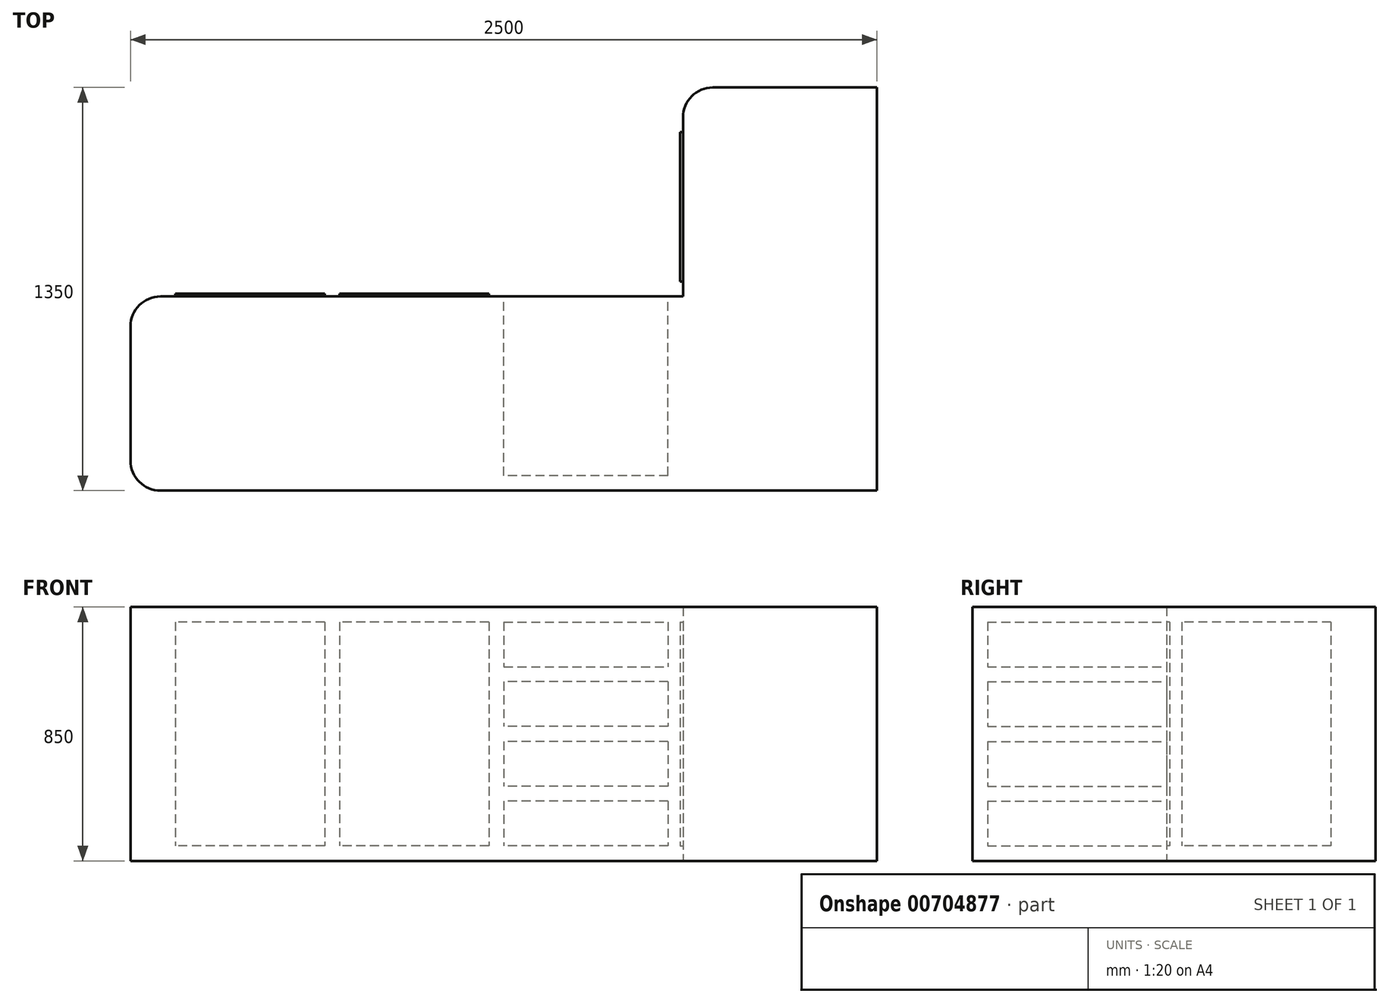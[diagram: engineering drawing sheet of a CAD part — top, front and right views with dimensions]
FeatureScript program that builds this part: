
annotation { "Feature Type Name" : "Feature", "Feature Type Description" : "" }
export const myFeature = defineFeature(function(context is Context, id is Id, definition is map)
    precondition{}
    {
        {
            var Q0;
            Q0=qCreatedBy(makeId("Top.planeOp"),FACE);
            var sketch = newSketch(context, id + "F0", { "sketchPlane" : qUnion([Q0])});
            skLineSegment(sketch, "E0", {"start": v(0, 0) * mm, "end": v(-2400, 0) * mm});
            skLineSegment(sketch, "E1", {"start": v(-2500, 100) * mm, "end": v(-2500, 550) * mm});
            skLineSegment(sketch, "E2", {"start": v(-2400, 650) * mm, "end": v(-650, 650) * mm});
            skLineSegment(sketch, "E3", {"start": v(-650, 650) * mm, "end": v(-650, 1250) * mm});
            skLineSegment(sketch, "E4", {"start": v(-550, 1350) * mm, "end": v(0, 1350) * mm});
            skLineSegment(sketch, "E5", {"start": v(0, 1350) * mm, "end": v(0, 0) * mm});
            skPoint(sketch, "E6.visualSharp", {"position": v(-650, 650) * mm});
            skPoint(sketch, "E7.visualSharp", {"position": v(-650, 1350) * mm});
            skArc(sketch, "E7.filletArc", {"start": v(-550, 1350) * mm, "mid": v(-620.71, 1320.71) * mm, "end": v(-650, 1250) * mm});
            skPoint(sketch, "E8.visualSharp", {"position": v(-2500, 650) * mm});
            skArc(sketch, "E8.filletArc", {"start": v(-2400, 650) * mm, "mid": v(-2470.71, 620.71) * mm, "end": v(-2500, 550) * mm});
            skPoint(sketch, "E9.visualSharp", {"position": v(-2500, 0) * mm});
            skArc(sketch, "E9.filletArc", {"start": v(-2500, 100) * mm, "mid": v(-2470.71, 29.29) * mm, "end": v(-2400, 0) * mm});
            skSolve(sketch);
        }
        {
            var Q0;
            Q0=makeQuery(id+"F0.imprint","IMPRINT",FACE,{"disambiguationData":[TD([[makeQuery(id+"F0.imprint","IMPRINT",EDGE,{"derivedFrom":sQuery(id+"F0.wireOp",EDGE,"E0")}),-1.0]])]});
            extrude(context, id + "F1", {"entities" : qUnion([Q0]), "depth" : 850 * mm, "offsetDistance" : 25 * mm});
        }
        {
            var Q0;
            Q0=makeQuery(id+"F1.opExtrude","SWEPT_FACE",FACE,{"disambiguationData":[OSD([sQuery(id+"F0.wireOp",EDGE,"E2")])]});
            var sketch = newSketch(context, id + "F2", { "sketchPlane" : qUnion([Q0])});
            skPoint(sketch, "E10.oppositeSnap0", {"position": v(1525, 0) * mm});
            skLineSegment(sketch, "E11.bottom", {"start": v(1300, 800) * mm, "end": v(1800, 800) * mm});
            skLineSegment(sketch, "E11.top", {"start": v(1300, 50) * mm, "end": v(1800, 50) * mm});
            skLineSegment(sketch, "E11.left", {"start": v(1300, 800) * mm, "end": v(1300, 50) * mm});
            skLineSegment(sketch, "E11.right", {"start": v(1800, 800) * mm, "end": v(1800, 50) * mm});
            skLineSegment(sketch, "E12.bottom", {"start": v(1850, 800) * mm, "end": v(2350, 800) * mm});
            skLineSegment(sketch, "E12.top", {"start": v(1850, 50) * mm, "end": v(2350, 50) * mm});
            skLineSegment(sketch, "E12.left", {"start": v(1850, 800) * mm, "end": v(1850, 50) * mm});
            skLineSegment(sketch, "E12.right", {"start": v(2350, 800) * mm, "end": v(2350, 50) * mm});
            skLineSegment(sketch, "E13.bottom", {"start": v(1250, 800) * mm, "end": v(700, 800) * mm});
            skLineSegment(sketch, "E13.top", {"start": v(1250, 650) * mm, "end": v(700, 650) * mm});
            skLineSegment(sketch, "E13.left", {"start": v(1250, 800) * mm, "end": v(1250, 650) * mm});
            skLineSegment(sketch, "E13.right", {"start": v(700, 800) * mm, "end": v(700, 650) * mm});
            skLineSegment(sketch, "E14.bottom", {"start": v(700, 600) * mm, "end": v(1250, 600) * mm});
            skLineSegment(sketch, "E14.top", {"start": v(700, 450) * mm, "end": v(1250, 450) * mm});
            skLineSegment(sketch, "E14.left", {"start": v(700, 600) * mm, "end": v(700, 450) * mm});
            skLineSegment(sketch, "E14.right", {"start": v(1250, 600) * mm, "end": v(1250, 450) * mm});
            skLineSegment(sketch, "E15.bottom", {"start": v(700, 400) * mm, "end": v(1250, 400) * mm});
            skLineSegment(sketch, "E15.top", {"start": v(700, 250) * mm, "end": v(1250, 250) * mm});
            skLineSegment(sketch, "E15.left", {"start": v(700, 400) * mm, "end": v(700, 250) * mm});
            skLineSegment(sketch, "E15.right", {"start": v(1250, 400) * mm, "end": v(1250, 250) * mm});
            skLineSegment(sketch, "E16.bottom", {"start": v(700, 200) * mm, "end": v(1250, 200) * mm});
            skLineSegment(sketch, "E16.top", {"start": v(700, 50) * mm, "end": v(1250, 50) * mm});
            skLineSegment(sketch, "E16.left", {"start": v(700, 200) * mm, "end": v(700, 50) * mm});
            skLineSegment(sketch, "E16.right", {"start": v(1250, 200) * mm, "end": v(1250, 50) * mm});
            skSolve(sketch);
        }
        {
            var Q0;
            Q0=makeQuery(id+"F1.opExtrude","SWEPT_FACE",FACE,{"disambiguationData":[OSD([sQuery(id+"F0.wireOp",EDGE,"E3")])]});
            var sketch = newSketch(context, id + "F3", { "sketchPlane" : qUnion([Q0])});
            skLineSegment(sketch, "E17.bottom", {"start": v(-1200, 800) * mm, "end": v(-700, 800) * mm});
            skLineSegment(sketch, "E17.top", {"start": v(-1200, 50) * mm, "end": v(-700, 50) * mm});
            skLineSegment(sketch, "E17.left", {"start": v(-1200, 800) * mm, "end": v(-1200, 50) * mm});
            skLineSegment(sketch, "E17.right", {"start": v(-700, 800) * mm, "end": v(-700, 50) * mm});
            skSolve(sketch);
        }
        {
            var Q0;
            Q0=makeQuery(id+"F2.imprint","IMPRINT",FACE,{"disambiguationData":[TD([[makeQuery(id+"F2.imprint","IMPRINT",EDGE,{"derivedFrom":sQuery(id+"F2.wireOp",EDGE,"E13.bottom")}),1.0]])]});
            var Q1;
            Q1=makeQuery(id+"F2.imprint","IMPRINT",FACE,{"disambiguationData":[TD([[makeQuery(id+"F2.imprint","IMPRINT",EDGE,{"derivedFrom":sQuery(id+"F2.wireOp",EDGE,"E14.bottom")}),-1.0]])]});
            var Q2;
            Q2=makeQuery(id+"F2.imprint","IMPRINT",FACE,{"disambiguationData":[TD([[makeQuery(id+"F2.imprint","IMPRINT",EDGE,{"derivedFrom":sQuery(id+"F2.wireOp",EDGE,"E15.bottom")}),-1.0]])]});
            var Q3;
            Q3=makeQuery(id+"F2.imprint","IMPRINT",FACE,{"disambiguationData":[TD([[makeQuery(id+"F2.imprint","IMPRINT",EDGE,{"derivedFrom":sQuery(id+"F2.wireOp",EDGE,"E16.bottom")}),-1.0]])]});
            extrude(context, id + "F4", {"entities" : qUnion([Q0, Q1, Q2, Q3]), "operationType" : NewBodyOperationType.REMOVE, "oppositeDirection" : true, "depth" : 600 * mm, "offsetDistance" : 25 * mm});
        }
        {
            var Q0;
            Q0=makeQuery(id+"F2.imprint","IMPRINT",FACE,{"disambiguationData":[TD([[makeQuery(id+"F2.imprint","IMPRINT",EDGE,{"derivedFrom":sQuery(id+"F2.wireOp",EDGE,"E11.bottom")}),-1.0]])]});
            var Q1;
            Q1=makeQuery(id+"F2.imprint","IMPRINT",FACE,{"disambiguationData":[TD([[makeQuery(id+"F2.imprint","IMPRINT",EDGE,{"derivedFrom":sQuery(id+"F2.wireOp",EDGE,"E12.bottom")}),-1.0]])]});
            extrude(context, id + "F5", {"entities" : qUnion([Q0, Q1]), "operationType" : NewBodyOperationType.ADD, "depth" : 10 * mm, "offsetDistance" : 25 * mm});
        }
        {
            var Q0;
            Q0=makeQuery(id+"F5.opExtrude","CAP_FACE",FACE,{"disambiguationData":[OSD([sQuery(id+"F2.wireOp",EDGE,"E12.bottom"),sQuery(id+"F2.wireOp",EDGE,"E12.top"),sQuery(id+"F2.wireOp",EDGE,"E12.left"),sQuery(id+"F2.wireOp",EDGE,"E12.right")])],"isStart":false});
            var sketch = newSketch(context, id + "F6", { "sketchPlane" : qUnion([Q0])});
            skLineSegment(sketch, "E18.bottom", {"start": v(1925, 750) * mm, "end": v(2025, 750) * mm});
            skLineSegment(sketch, "E18.top", {"start": v(1925, 700) * mm, "end": v(2025, 700) * mm});
            skLineSegment(sketch, "E18.left", {"start": v(1900, 725) * mm, "end": v(1900, 725) * mm});
            skLineSegment(sketch, "E18.right", {"start": v(2050, 725) * mm, "end": v(2050, 725) * mm});
            skPoint(sketch, "E19.visualSharp", {"position": v(1900, 750) * mm});
            skArc(sketch, "E19.filletArc", {"start": v(1925, 750) * mm, "mid": v(1907.32, 742.68) * mm, "end": v(1900, 725) * mm});
            skPoint(sketch, "E20.visualSharp", {"position": v(1900, 700) * mm});
            skArc(sketch, "E20.filletArc", {"start": v(1900, 725) * mm, "mid": v(1907.32, 707.32) * mm, "end": v(1925, 700) * mm});
            skPoint(sketch, "E21.visualSharp", {"position": v(2050, 750) * mm});
            skArc(sketch, "E21.filletArc", {"start": v(2050, 725) * mm, "mid": v(2042.68, 742.68) * mm, "end": v(2025, 750) * mm});
            skPoint(sketch, "E22.visualSharp", {"position": v(2050, 700) * mm});
            skArc(sketch, "E22.filletArc", {"start": v(2025, 700) * mm, "mid": v(2042.68, 707.32) * mm, "end": v(2050, 725) * mm});
            skSolve(sketch);
        }
        {
            var Q0;
            Q0=makeQuery(id+"F5.opExtrude","CAP_FACE",FACE,{"disambiguationData":[OSD([sQuery(id+"F2.wireOp",EDGE,"E11.bottom"),sQuery(id+"F2.wireOp",EDGE,"E11.top"),sQuery(id+"F2.wireOp",EDGE,"E11.left"),sQuery(id+"F2.wireOp",EDGE,"E11.right")])],"isStart":false});
            var sketch = newSketch(context, id + "F7", { "sketchPlane" : qUnion([Q0])});
            skLineSegment(sketch, "E23.bottom", {"start": v(1625, 750) * mm, "end": v(1725, 750) * mm});
            skLineSegment(sketch, "E23.top", {"start": v(1625, 700) * mm, "end": v(1725, 700) * mm});
            skLineSegment(sketch, "E23.left", {"start": v(1600, 725) * mm, "end": v(1600, 725) * mm});
            skLineSegment(sketch, "E23.right", {"start": v(1750, 725) * mm, "end": v(1750, 725) * mm});
            skPoint(sketch, "E24.visualSharp", {"position": v(1600, 750) * mm});
            skArc(sketch, "E24.filletArc", {"start": v(1625, 750) * mm, "mid": v(1607.32, 742.68) * mm, "end": v(1600, 725) * mm});
            skPoint(sketch, "E25.visualSharp", {"position": v(1600, 700) * mm});
            skArc(sketch, "E25.filletArc", {"start": v(1600, 725) * mm, "mid": v(1607.32, 707.32) * mm, "end": v(1625, 700) * mm});
            skPoint(sketch, "E26.visualSharp", {"position": v(1750, 750) * mm});
            skArc(sketch, "E26.filletArc", {"start": v(1750, 725) * mm, "mid": v(1742.68, 742.68) * mm, "end": v(1725, 750) * mm});
            skPoint(sketch, "E27.visualSharp", {"position": v(1750, 700) * mm});
            skArc(sketch, "E27.filletArc", {"start": v(1725, 700) * mm, "mid": v(1742.68, 707.32) * mm, "end": v(1750, 725) * mm});
            skSolve(sketch);
        }
        {
            var Q0;
            Q0=makeQuery(id+"F3.imprint","IMPRINT",FACE,{"disambiguationData":[TD([[makeQuery(id+"F3.imprint","IMPRINT",EDGE,{"derivedFrom":sQuery(id+"F3.wireOp",EDGE,"E17.bottom")}),-1.0]])]});
            extrude(context, id + "F8", {"entities" : qUnion([Q0]), "operationType" : NewBodyOperationType.ADD, "depth" : 10 * mm, "offsetDistance" : 25 * mm});
        }
    });
